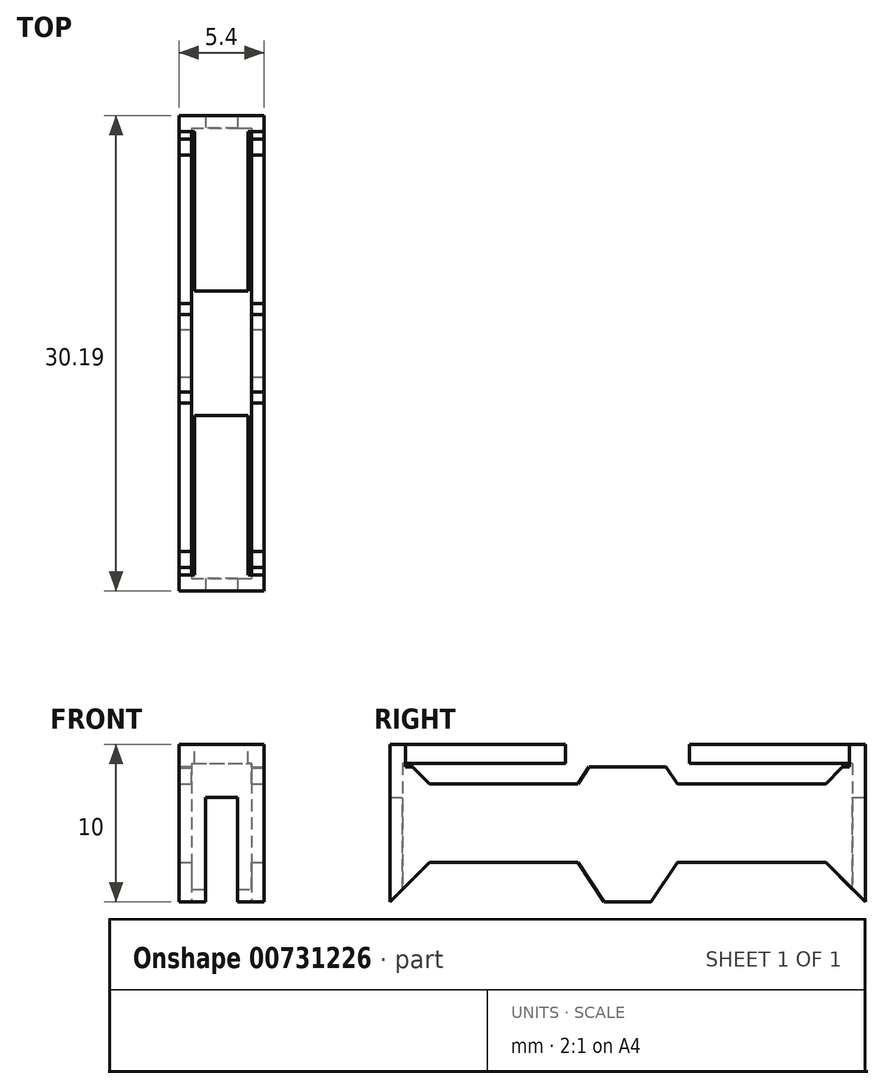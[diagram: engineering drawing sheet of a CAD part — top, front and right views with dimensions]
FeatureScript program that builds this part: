
annotation { "Feature Type Name" : "Feature", "Feature Type Description" : "" }
export const myFeature = defineFeature(function(context is Context, id is Id, definition is map)
    precondition{}
    {
        {
            var Q0;
            Q0=qCreatedBy(makeId("Top.planeOp"),FACE);
            var sketch = newSketch(context, id + "F0", { "sketchPlane" : qUnion([Q0])});
            skLineSegment(sketch, "E0.bottom", {"start": v(0, 0) * mm, "end": v(-5.4, 0) * mm});
            skLineSegment(sketch, "E0.top", {"start": v(0, 30.19) * mm, "end": v(-5.4, 30.19) * mm});
            skLineSegment(sketch, "E0.left", {"start": v(0, 0) * mm, "end": v(0, 30.19) * mm});
            skLineSegment(sketch, "E0.right", {"start": v(-5.4, 0) * mm, "end": v(-5.4, 30.19) * mm});
            skLineSegment(sketch, "E1.0", {"start": v(-0.8, 0.8) * mm, "end": v(-0.8, 29.39) * mm});
            skLineSegment(sketch, "E1.1", {"start": v(-0.8, 0.8) * mm, "end": v(-4.6, 0.8) * mm});
            skLineSegment(sketch, "E1.2", {"start": v(-4.6, 0.8) * mm, "end": v(-4.6, 29.39) * mm});
            skLineSegment(sketch, "E1.3", {"start": v(-0.8, 29.39) * mm, "end": v(-4.6, 29.39) * mm});
            skSolve(sketch);
        }
        {
            var Q0;
            Q0 = qSketchRegion(id + "F0", true);
            extrude(context, id + "F1", {"entities" : qUnion([Q0]), "depth" : 10 * mm, "offsetDistance" : 25 * mm});
        }
        {
            var Q0;
            Q0=makeQuery(id+"F1.opExtrude","SWEPT_FACE",FACE,{"disambiguationData":[OSD([sQuery(id+"F0.wireOp",EDGE,"E0.left")])]});
            var sketch = newSketch(context, id + "F2", { "sketchPlane" : qUnion([Q0])});
            skLineSegment(sketch, "E2", {"start": v(0, 5) * mm, "end": v(30.19, 5) * mm});
            skLineSegment(sketch, "E3", {"start": v(15.1, 5) * mm, "end": v(15.1, 0) * mm});
            skLineSegment(sketch, "E4", {"start": v(15.1, 5) * mm, "end": v(15.1, 10) * mm});
            skLineSegment(sketch, "E5.1", {"start": v(1.5, 8.5) * mm, "end": v(1.5, 1.5) * mm});
            skLineSegment(sketch, "E5.3", {"start": v(28.69, 1.5) * mm, "end": v(28.69, 8.5) * mm});
            skLineSegment(sketch, "E6.0", {"start": v(2.5, 2.5) * mm, "end": v(27.69, 2.5) * mm});
            skLineSegment(sketch, "E6.1", {"start": v(2.5, 7.5) * mm, "end": v(2.5, 2.5) * mm});
            skLineSegment(sketch, "E6.2", {"start": v(27.69, 7.5) * mm, "end": v(2.5, 7.5) * mm});
            skLineSegment(sketch, "E6.3", {"start": v(27.69, 2.5) * mm, "end": v(27.69, 7.5) * mm});
            skLineSegment(sketch, "E7", {"start": v(28.69, 1.5) * mm, "end": v(27.69, 2.5) * mm});
            skLineSegment(sketch, "E8", {"start": v(1.5, 1.5) * mm, "end": v(2.5, 2.5) * mm});
            skLineSegment(sketch, "E9", {"start": v(1.5, 1.5) * mm, "end": v(0, 0) * mm});
            skLineSegment(sketch, "E10", {"start": v(28.69, 1.5) * mm, "end": v(30.19, 0) * mm});
            skLineSegment(sketch, "E11", {"start": v(15.1, 0) * mm, "end": v(16.6, 0) * mm});
            skLineSegment(sketch, "E12", {"start": v(15.1, 0) * mm, "end": v(13.6, 0) * mm});
            skLineSegment(sketch, "E13", {"start": v(16.6, 0) * mm, "end": v(18.27, 2.5) * mm});
            skLineSegment(sketch, "E14", {"start": v(13.6, 0) * mm, "end": v(11.93, 2.5) * mm});
            skLineSegment(sketch, "E15", {"start": v(28.69, 1.5) * mm, "end": v(30.19, 1.5) * mm});
            skLineSegment(sketch, "E16", {"start": v(1.5, 1.5) * mm, "end": v(0, 1.5) * mm});
            skLineSegment(sketch, "E17", {"start": v(28.69, 8.5) * mm, "end": v(30.19, 8.5) * mm});
            skLineSegment(sketch, "E18", {"start": v(28.69, 8.5) * mm, "end": v(27.69, 7.5) * mm});
            skLineSegment(sketch, "E19", {"start": v(2.5, 7.5) * mm, "end": v(1.5, 8.5) * mm});
            skLineSegment(sketch, "E20", {"start": v(0, 8.5) * mm, "end": v(1.5, 8.5) * mm});
            skLineSegment(sketch, "E21", {"start": v(15.1, 10) * mm, "end": v(16.6, 10) * mm});
            skLineSegment(sketch, "E22", {"start": v(15.1, 10) * mm, "end": v(13.6, 10) * mm});
            skLineSegment(sketch, "E23", {"start": v(16.6, 10) * mm, "end": v(18.27, 7.5) * mm});
            skLineSegment(sketch, "E24", {"start": v(13.6, 10) * mm, "end": v(11.93, 7.5) * mm});
            skLineSegment(sketch, "E25", {"start": v(28.69, 8.5) * mm, "end": v(28.69, 10) * mm});
            skLineSegment(sketch, "E26", {"start": v(1.5, 8.5) * mm, "end": v(1.5, 10) * mm});
            skSolve(sketch);
        }
        {
            var Q0;
            Q0=makeQuery(id+"F1.opExtrude","SWEPT_FACE",FACE,{"disambiguationData":[OSD([sQuery(id+"F0.wireOp",EDGE,"E0.top")])]});
            var sketch = newSketch(context, id + "F3", { "sketchPlane" : qUnion([Q0])});
            skLineSegment(sketch, "E27.bottom", {"start": v(3.72, 6.62) * mm, "end": v(1.68, 6.62) * mm});
            skLineSegment(sketch, "E27.top", {"start": v(3.72, -6.62) * mm, "end": v(1.68, -6.62) * mm});
            skLineSegment(sketch, "E27.left", {"start": v(3.72, 6.62) * mm, "end": v(3.72, -6.62) * mm});
            skLineSegment(sketch, "E27.right", {"start": v(1.68, 6.62) * mm, "end": v(1.68, -6.62) * mm});
            skPoint(sketch, "E27.middle", {"position": v(2.7, 0) * mm});
            skLineSegment(sketch, "E28.bottom", {"start": v(0, 10) * mm, "end": v(5.4, 10) * mm});
            skLineSegment(sketch, "E28.top", {"start": v(0, 8.8) * mm, "end": v(5.4, 8.8) * mm});
            skLineSegment(sketch, "E28.left", {"start": v(0, 10) * mm, "end": v(0, 8.8) * mm});
            skLineSegment(sketch, "E28.right", {"start": v(5.4, 10) * mm, "end": v(5.4, 8.8) * mm});
            skSolve(sketch);
        }
        {
            var Q0;
            {var subQ4=sQuery(id+"F2.wireOp",EDGE,"E7");Q0=makeQuery(id+"F2.imprint","IMPRINT",FACE,{"disambiguationData":[TD([[makeQuery(id+"F2.imprint","IMPRINT",EDGE,{"derivedFrom":subQ4}),1.0]])]});}
            var Q1;
            {var subQ2=sQuery(id+"F2.wireOp",EDGE,"E8");Q1=makeQuery(id+"F2.imprint","IMPRINT",FACE,{"disambiguationData":[TD([[makeQuery(id+"F2.imprint","IMPRINT",EDGE,{"derivedFrom":subQ2}),-1.0]])]});}
            extrude(context, id + "F4", {"entities" : qUnion([Q0, Q1]), "operationType" : NewBodyOperationType.REMOVE, "oppositeDirection" : true, "depth" : 6.7 * mm, "offsetDistance" : 25 * mm});
        }
        {
            var Q0;
            {var subQ0=sQuery(id+"F3.wireOp",EDGE,"E27.bottom");Q0=makeQuery(id+"F3.imprint","IMPRINT",FACE,{"disambiguationData":[TD([[makeQuery(id+"F3.imprint","IMPRINT",EDGE,{"derivedFrom":subQ0}),1.0]])]});}
            extrude(context, id + "F5", {"entities" : qUnion([Q0]), "operationType" : NewBodyOperationType.REMOVE, "oppositeDirection" : true, "depth" : 31.8 * mm, "offsetDistance" : 25 * mm});
        }
        {
            var Q0;
            {var subQ2=sQuery(id+"F2.wireOp",EDGE,"E18");Q0=makeQuery(id+"F2.imprint","IMPRINT",FACE,{"disambiguationData":[TD([[makeQuery(id+"F2.imprint","IMPRINT",EDGE,{"derivedFrom":subQ2}),-1.0]])]});}
            var Q1;
            {var subQ1=sQuery(id+"F2.wireOp",EDGE,"E19");Q1=makeQuery(id+"F2.imprint","IMPRINT",FACE,{"disambiguationData":[TD([[makeQuery(id+"F2.imprint","IMPRINT",EDGE,{"derivedFrom":subQ1}),-1.0]])]});}
            extrude(context, id + "F6", {"entities" : qUnion([Q0, Q1]), "operationType" : NewBodyOperationType.REMOVE, "oppositeDirection" : true, "depth" : 6.5 * mm, "offsetDistance" : 25 * mm});
        }
        {
            var Q0;
            Q0=makeQuery(id+"F3.imprint","IMPRINT",FACE,{"disambiguationData":[TD([[makeQuery(id+"F3.imprint","IMPRINT",EDGE,{"derivedFrom":sQuery(id+"F3.wireOp",EDGE,"E28.bottom")}),-1.0]])]});
            extrude(context, id + "F7", {"entities" : qUnion([Q0]), "operationType" : NewBodyOperationType.ADD, "oppositeDirection" : true, "depth" : 6.9 * mm, "offsetDistance" : 25 * mm});
        }
        {
            var Q0;
            Q0=makeQuery(id+"F3.imprint","IMPRINT",FACE,{"disambiguationData":[TD([[makeQuery(id+"F3.imprint","IMPRINT",EDGE,{"derivedFrom":sQuery(id+"F3.wireOp",EDGE,"E28.bottom")}),-1.0]])]});
            extrude(context, id + "F8", {"entities" : qUnion([Q0]), "operationType" : NewBodyOperationType.ADD, "oppositeDirection" : true, "depth" : 30.1 * mm, "offsetDistance" : 25 * mm});
        }
        {
            var Q0;
            {var subQ0=sQuery(id+"F3.wireOp",EDGE,"E28.bottom");var subQ1=sQuery(id+"F0.wireOp",EDGE,"E1.0");var subQ2=makeQuery(id+"F1.opExtrude","SWEPT_FACE",FACE,{"disambiguationData":[OSD([subQ1])]});var subQ3=sQuery(id+"F0.wireOp",EDGE,"E0.right");var subQ4=makeQuery(id+"F1.opExtrude","SWEPT_FACE",FACE,{"disambiguationData":[OSD([subQ3])]});var subQ5=sQuery(id+"F0.wireOp",EDGE,"E0.left");var subQ6=makeQuery(id+"F1.opExtrude","SWEPT_FACE",FACE,{"disambiguationData":[OSD([subQ5])]});var subQ7=sQuery(id+"F0.wireOp",EDGE,"E0.top");var subQ8=sQuery(id+"F0.wireOp",EDGE,"E1.2");var subQ9=makeQuery(id+"F1.opExtrude","SWEPT_FACE",FACE,{"disambiguationData":[OSD([subQ8])]});var subQ10=sQuery(id+"F0.wireOp",EDGE,"E1.3");var subQ11=sQuery(id+"F0.wireOp",EDGE,"E1.1");var subQ12=sQuery(id+"F0.wireOp",EDGE,"E0.bottom");var subQ13=makeQuery(id+"F1.opExtrude","CAP_FACE",FACE,{"disambiguationData":[OSD([subQ12,subQ7,subQ5,subQ3,subQ1,subQ11,subQ8,subQ10])],"isStart":false});var subQ14=makeQuery(id+"F6.opExtrude","SWEPT_FACE",FACE,{"disambiguationData":[OSD([sQuery(id+"F2.wireOp",EDGE,"E24")])]});var subQ15=makeQuery(id+"F6.opExtrude","SWEPT_FACE",FACE,{"disambiguationData":[OSD([sQuery(id+"F2.wireOp",EDGE,"E23")])]});Q0=makeQuery(id+"F8.boolean.opBoolean","MERGE",FACE,{"derivedFrom":[makeQuery(id+"F6.boolean.opBoolean","SPLIT",FACE,{"disambiguationData":[TD([subQ6,subQ2,subQ15,subQ14])],"derivedFrom":subQ13}),makeQuery(id+"F6.boolean.opBoolean","SPLIT",FACE,{"disambiguationData":[TD([subQ4,subQ9,subQ15,subQ14])],"derivedFrom":subQ13}),makeQuery(id+"F6.boolean.opBoolean","SPLIT",FACE,{"disambiguationData":[TD([makeQuery(id+"F1.opExtrude","SWEPT_FACE",FACE,{"disambiguationData":[OSD([subQ12])]}),subQ6,subQ4,subQ2,makeQuery(id+"F1.opExtrude","SWEPT_FACE",FACE,{"disambiguationData":[OSD([subQ11])]}),subQ9,makeQuery(id+"F6.opExtrude","SWEPT_FACE",FACE,{"disambiguationData":[OSD([sQuery(id+"F2.wireOp",EDGE,"E26")])]})])],"derivedFrom":subQ13}),makeQuery(id+"F7.boolean.opBoolean","MERGE",FACE,{"derivedFrom":[makeQuery(id+"F6.boolean.opBoolean","SPLIT",FACE,{"disambiguationData":[TD([makeQuery(id+"F1.opExtrude","SWEPT_FACE",FACE,{"disambiguationData":[OSD([subQ7])]}),subQ6,subQ4,subQ2,subQ9,makeQuery(id+"F1.opExtrude","SWEPT_FACE",FACE,{"disambiguationData":[OSD([subQ10])]}),makeQuery(id+"F6.opExtrude","SWEPT_FACE",FACE,{"disambiguationData":[OSD([sQuery(id+"F2.wireOp",EDGE,"E25")])]})])],"derivedFrom":subQ13}),makeQuery(id+"F7.opExtrude","SWEPT_FACE",FACE,{"disambiguationData":[OSD([subQ0])]})]}),makeQuery(id+"F8.opExtrude","SWEPT_FACE",FACE,{"disambiguationData":[OSD([subQ0])]})]});}
            var sketch = newSketch(context, id + "F9", { "sketchPlane" : qUnion([Q0])});
            skLineSegment(sketch, "E29.0", {"start": v(-1, 1) * mm, "end": v(-1, 29.19) * mm});
            skLineSegment(sketch, "E29.1", {"start": v(-4.4, 1) * mm, "end": v(-1, 1) * mm});
            skLineSegment(sketch, "E29.2", {"start": v(-4.4, 29.19) * mm, "end": v(-4.4, 1) * mm});
            skLineSegment(sketch, "E29.3", {"start": v(-1, 29.19) * mm, "end": v(-4.4, 29.19) * mm});
            skLineSegment(sketch, "E30", {"start": v(-4.4, 29.19) * mm, "end": v(-4.4, 30.19) * mm});
            skLineSegment(sketch, "E31", {"start": v(-1, 29.19) * mm, "end": v(-1, 30.19) * mm});
            skPoint(sketch, "E31.endSnap0", {"position": v(-2.7, 30.19) * mm});
            skLineSegment(sketch, "E32", {"start": v(-4.4, 1) * mm, "end": v(-4.4, 0) * mm});
            skLineSegment(sketch, "E33", {"start": v(-1, 1) * mm, "end": v(-1, 0) * mm});
            skLineSegment(sketch, "E34", {"start": v(-1, 1) * mm, "end": v(0, 1) * mm});
            skLineSegment(sketch, "E35", {"start": v(-4.4, 1) * mm, "end": v(-5.4, 1) * mm});
            skLineSegment(sketch, "E36", {"start": v(-1, 29.19) * mm, "end": v(0, 29.19) * mm});
            skLineSegment(sketch, "E37", {"start": v(-4.4, 29.19) * mm, "end": v(-5.4, 29.19) * mm});
            skLineSegment(sketch, "E38", {"start": v(-4.4, 15.1) * mm, "end": v(-1, 15.1) * mm});
            skLineSegment(sketch, "E39.bottom", {"start": v(-1, 19.03) * mm, "end": v(-4.4, 19.03) * mm});
            skLineSegment(sketch, "E39.top", {"start": v(-1, 11.15) * mm, "end": v(-4.4, 11.15) * mm});
            skLineSegment(sketch, "E39.left", {"start": v(-1, 19.03) * mm, "end": v(-1, 11.15) * mm});
            skLineSegment(sketch, "E39.right", {"start": v(-4.4, 19.03) * mm, "end": v(-4.4, 11.15) * mm});
            skPoint(sketch, "E39.middle", {"position": v(-2.7, 15.1) * mm});
            skSolve(sketch);
        }
        {
            var Q0;
            Q0=makeQuery(id+"F9.imprint","IMPRINT",FACE,{"disambiguationData":[TD([[makeQuery(id+"F9.imprint","IMPRINT",EDGE,{"derivedFrom":sQuery(id+"F9.wireOp",EDGE,"E29.2")}),-1.0]])]});
            var Q1;
            Q1=makeQuery(id+"F9.imprint","IMPRINT",FACE,{"disambiguationData":[TD([[makeQuery(id+"F9.imprint","IMPRINT",EDGE,{"derivedFrom":sQuery(id+"F9.wireOp",EDGE,"E29.0")}),-1.0]])]});
            extrude(context, id + "F10", {"entities" : qUnion([Q0, Q1]), "operationType" : NewBodyOperationType.REMOVE, "oppositeDirection" : true, "depth" : 1.42 * mm, "offsetDistance" : 25 * mm});
        }
        {
            var Q0;
            {var subQ0=sQuery(id+"F9.wireOp",EDGE,"E38");Q0=makeQuery(id+"F9.imprint","IMPRINT",FACE,{"disambiguationData":[TD([[makeQuery(id+"F9.imprint","IMPRINT",EDGE,{"derivedFrom":subQ0}),-1.0]])]});}
            var Q1;
            {var subQ0=sQuery(id+"F9.wireOp",EDGE,"E38");Q1=makeQuery(id+"F9.imprint","IMPRINT",FACE,{"disambiguationData":[TD([[makeQuery(id+"F9.imprint","IMPRINT",EDGE,{"derivedFrom":subQ0}),1.0]])]});}
            extrude(context, id + "F11", {"entities" : qUnion([Q0, Q1]), "operationType" : NewBodyOperationType.REMOVE, "oppositeDirection" : true, "depth" : 1.3 * mm, "offsetDistance" : 25 * mm});
        }
    });
